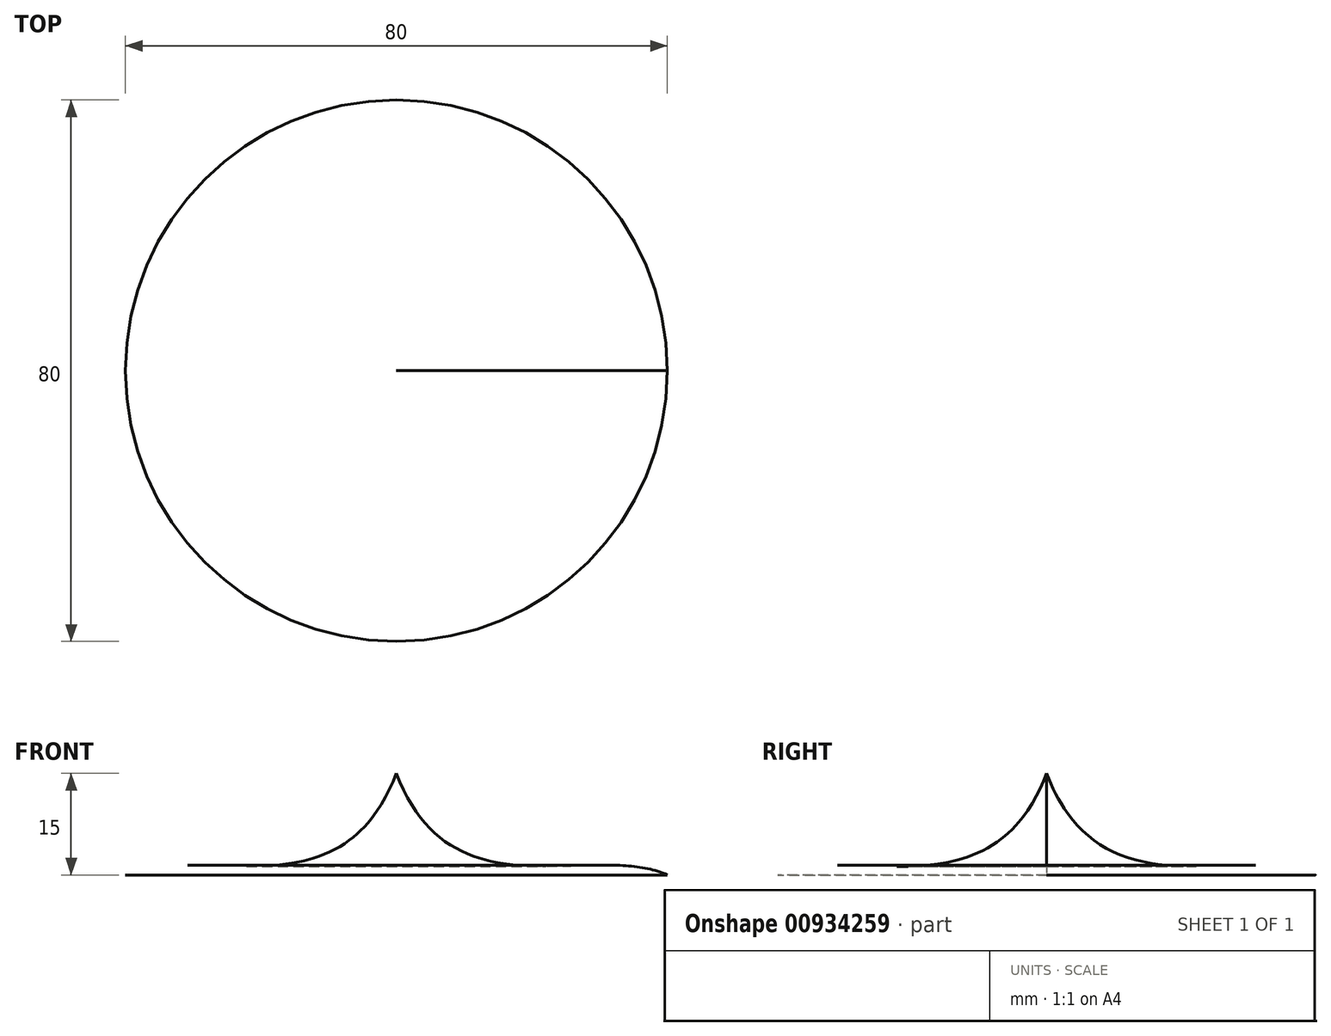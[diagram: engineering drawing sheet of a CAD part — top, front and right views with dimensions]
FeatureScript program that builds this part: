
annotation { "Feature Type Name" : "Feature", "Feature Type Description" : "" }
export const myFeature = defineFeature(function(context is Context, id is Id, definition is map)
    precondition{}
    {
        {
            var Q0;
            Q0=qCreatedBy(makeId("Front.planeOp"),FACE);
            var sketch = newSketch(context, id + "F0", { "sketchPlane" : qUnion([Q0])});
            skLineSegment(sketch, "E0", {"start": v(0, 15) * mm, "end": v(0, 85) * mm, "construction": true});
            skLineSegment(sketch, "E1", {"start": v(40, 0) * mm, "end": v(58.34, 0) * mm, "construction": true});
            skPoint(sketch, "E2.visualSharp", {"position": v(0, 0) * mm});
            skLineSegment(sketch, "E3", {"start": v(0, 15) * mm, "end": v(0, 0) * mm});
            skLineSegment(sketch, "E4", {"start": v(0, 0) * mm, "end": v(40, 0) * mm});
            skFitSpline(sketch, "E5", {"points": [v(0, 15) * mm, v(40, 0) * mm], "startDerivative": vector(24.32, -64.17) * mm, "endDerivative": vector(32.97, -15.05) * mm});
            skSolve(sketch);
        }
        {
            var Q0;
            Q0 = qSketchRegion(id + "F0", true);
            var Q1;
            Q1=sQuery(id+"F0.wireOp",EDGE,"E0");
            revolve(context, id + "F1", {"surfaceOperationType" : NewSurfaceOperationType.NEW, "entities" : qUnion([Q0]), "axis" : qUnion([Q1]), "revolveType" : RevolveType.FULL});
        }
    });
